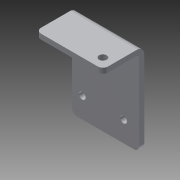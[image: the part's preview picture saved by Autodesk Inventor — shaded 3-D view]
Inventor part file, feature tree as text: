
AUTODESK INVENTOR PART (.ipt)
format: ipt  version: 2014 (Build 180170000, 170)  size: 122,368 bytes
history: native  units: in
note: dims shown in document units (in); Inventor stores cm internally (conversion verified against a paired STEP export)
features: sheet_metal_op x4, sketch x3, other x3, fillet x1
ambient origin geometry x8: Origin, YZ Plane, XZ Plane, XY Plane, X Axis, Y Axis, Z Axis, Center Point
bodies: Solid1 (feature_tree)
feature tree (11):
  sheet_metal_op  "Face1"
  sheet_metal_op  "Flange1"
  fillet  "Fillet1"  Radius=1.625in
  sketch  "Sketch1"  dims[d1=2.0in]
  other  "Plate1"
  sketch  "Sketch2"  dims[d2=0.163in]
  other  "Plate2"
  sheet_metal_op  "Bend1"
  sheet_metal_op  "Corner1"
  sketch  "Sketch4"  dims[d3=0.25in d4=0.7874in d6=1.0in d7=0.3937in d9=1.0in d11=0.125in d12=0.125in d13=0.0625in d14=0.25in d15=0.125in d16=1.0in d17=90.0deg d18=0.05in d19=0.5in d20=0.125in d21=0.125in d22=0.5in d28=0.187in d29=0.25in d30=0.25in d31=0.125in d32=0.0in d33=0.125in]
  other  "Cut2"
